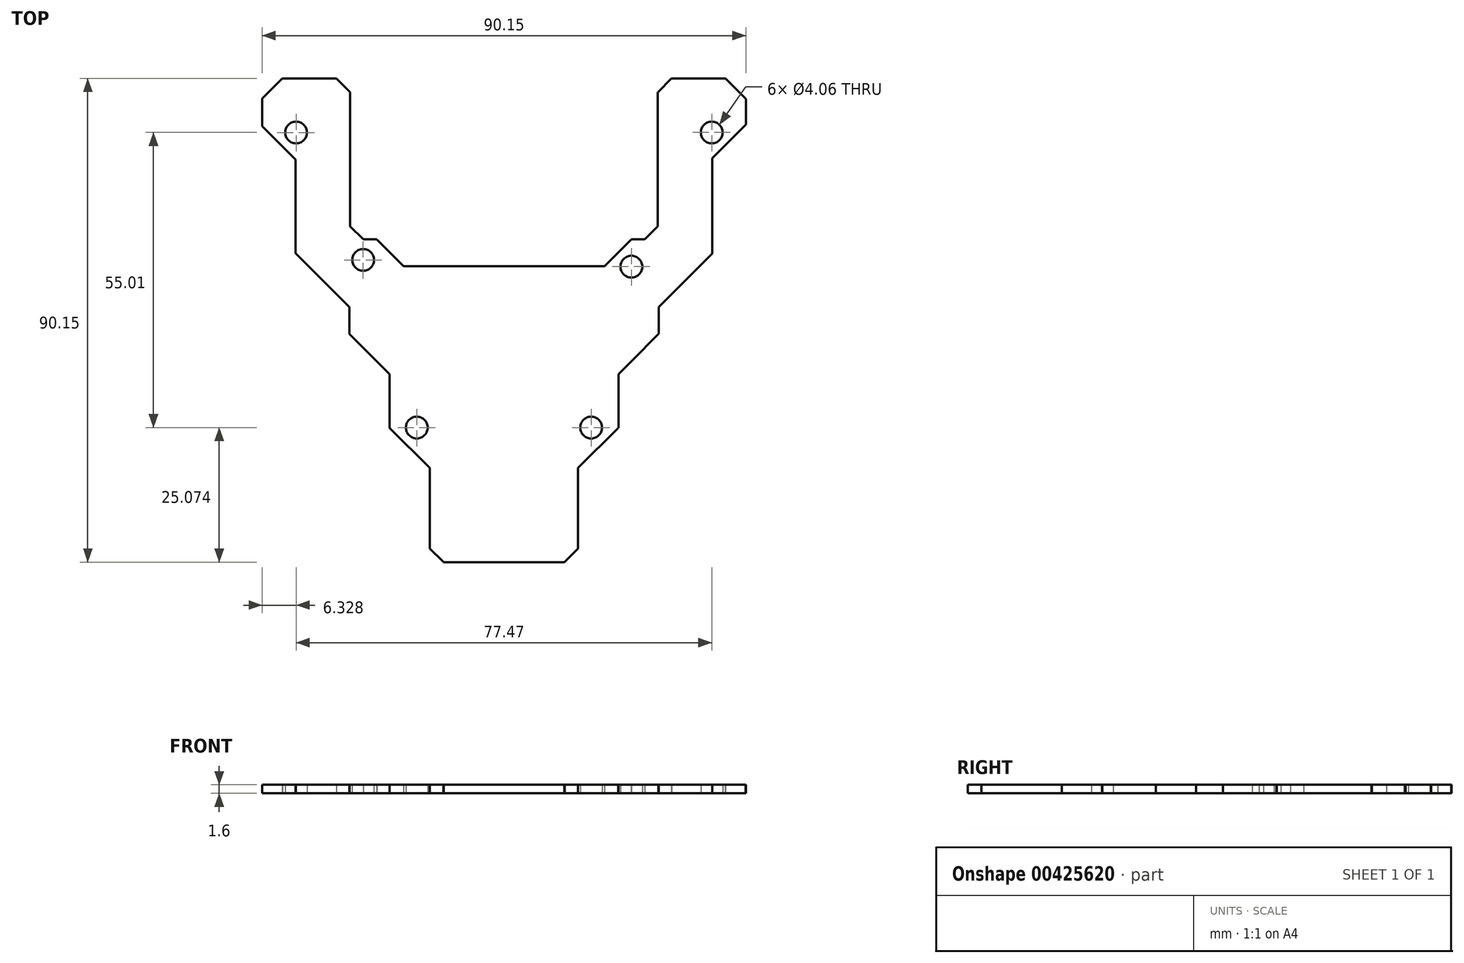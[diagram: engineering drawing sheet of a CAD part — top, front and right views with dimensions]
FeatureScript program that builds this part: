
annotation { "Feature Type Name" : "Feature", "Feature Type Description" : "" }
export const myFeature = defineFeature(function(context is Context, id is Id, definition is map)
    precondition{}
    {
        {
            var Q0;
            Q0=qCreatedBy(makeId("Top.planeOp"),FACE);
            var sketch = newSketch(context, id + "F0", { "sketchPlane" : qUnion([Q0])});
            skCircle(sketch, "E0", {"center": v(38.73, 22.84) * mm, "radius": 2.03 * mm});
            skCircle(sketch, "E1", {"center": v(23.76, -2.17) * mm, "radius": 2.03 * mm});
            skCircle(sketch, "E2", {"center": v(16.26, -32.17) * mm, "radius": 2.03 * mm});
            skCircle(sketch, "E3", {"center": v(-16.24, -32.17) * mm, "radius": 2.03 * mm});
            skCircle(sketch, "E4", {"center": v(-26.24, -0.92) * mm, "radius": 2.03 * mm});
            skCircle(sketch, "E5", {"center": v(-38.74, 22.83) * mm, "radius": 2.03 * mm});
            skLineSegment(sketch, "E6", {"start": v(-31.24, 32.9) * mm, "end": v(-31.24, 32.9) * mm});
            skLineSegment(sketch, "E7", {"start": v(-41.24, 32.9) * mm, "end": v(-31.24, 32.9) * mm});
            skLineSegment(sketch, "E8", {"start": v(-41.24, 32.9) * mm, "end": v(-41.24, 32.9) * mm});
            skLineSegment(sketch, "E9", {"start": v(-41.25, 32.9) * mm, "end": v(-41.24, 32.9) * mm});
            skLineSegment(sketch, "E10", {"start": v(-41.26, 32.9) * mm, "end": v(-41.25, 32.9) * mm});
            skLineSegment(sketch, "E11", {"start": v(-41.27, 32.9) * mm, "end": v(-41.26, 32.9) * mm});
            skLineSegment(sketch, "E12", {"start": v(-41.27, 32.9) * mm, "end": v(-41.27, 32.9) * mm});
            skLineSegment(sketch, "E13", {"start": v(-41.28, 32.9) * mm, "end": v(-41.27, 32.9) * mm});
            skLineSegment(sketch, "E14", {"start": v(-41.29, 32.9) * mm, "end": v(-41.28, 32.9) * mm});
            skLineSegment(sketch, "E15", {"start": v(-41.3, 32.89) * mm, "end": v(-41.29, 32.9) * mm});
            skLineSegment(sketch, "E16", {"start": v(-41.3, 32.89) * mm, "end": v(-41.3, 32.89) * mm});
            skLineSegment(sketch, "E17", {"start": v(-45.04, 29.14) * mm, "end": v(-41.3, 32.89) * mm});
            skLineSegment(sketch, "E18", {"start": v(-45.05, 29.13) * mm, "end": v(-45.04, 29.14) * mm});
            skLineSegment(sketch, "E19", {"start": v(-45.05, 29.13) * mm, "end": v(-45.05, 29.13) * mm});
            skLineSegment(sketch, "E20", {"start": v(-45.05, 29.12) * mm, "end": v(-45.05, 29.13) * mm});
            skLineSegment(sketch, "E21", {"start": v(-45.06, 29.12) * mm, "end": v(-45.05, 29.12) * mm});
            skLineSegment(sketch, "E22", {"start": v(-45.06, 29.11) * mm, "end": v(-45.06, 29.12) * mm});
            skLineSegment(sketch, "E23", {"start": v(-45.06, 29.11) * mm, "end": v(-45.06, 29.11) * mm});
            skLineSegment(sketch, "E24", {"start": v(-45.06, 29.1) * mm, "end": v(-45.06, 29.11) * mm});
            skLineSegment(sketch, "E25", {"start": v(-45.07, 29.1) * mm, "end": v(-45.06, 29.1) * mm});
            skLineSegment(sketch, "E26", {"start": v(-45.07, 29.09) * mm, "end": v(-45.07, 29.1) * mm});
            skLineSegment(sketch, "E27", {"start": v(-45.07, 29.08) * mm, "end": v(-45.07, 29.09) * mm});
            skLineSegment(sketch, "E28", {"start": v(-45.07, 24.08) * mm, "end": v(-45.07, 29.08) * mm});
            skLineSegment(sketch, "E29", {"start": v(-45.07, 24.08) * mm, "end": v(-45.07, 24.08) * mm});
            skLineSegment(sketch, "E30", {"start": v(-45.06, 24.07) * mm, "end": v(-45.07, 24.08) * mm});
            skLineSegment(sketch, "E31", {"start": v(-45.06, 24.06) * mm, "end": v(-45.06, 24.07) * mm});
            skLineSegment(sketch, "E32", {"start": v(-45.06, 24.06) * mm, "end": v(-45.06, 24.06) * mm});
            skLineSegment(sketch, "E33", {"start": v(-45.06, 24.05) * mm, "end": v(-45.06, 24.06) * mm});
            skLineSegment(sketch, "E34", {"start": v(-45.05, 24.04) * mm, "end": v(-45.06, 24.05) * mm});
            skLineSegment(sketch, "E35", {"start": v(-45.05, 24.04) * mm, "end": v(-45.05, 24.04) * mm});
            skLineSegment(sketch, "E36", {"start": v(-45.05, 24.03) * mm, "end": v(-45.05, 24.04) * mm});
            skLineSegment(sketch, "E37", {"start": v(-45.04, 24.03) * mm, "end": v(-45.05, 24.03) * mm});
            skLineSegment(sketch, "E38", {"start": v(-38.82, 17.8) * mm, "end": v(-45.04, 24.03) * mm});
            skLineSegment(sketch, "E39", {"start": v(-38.82, 0.33) * mm, "end": v(-38.82, 17.8) * mm});
            skLineSegment(sketch, "E40", {"start": v(-38.82, 0.33) * mm, "end": v(-38.82, 0.33) * mm});
            skLineSegment(sketch, "E41", {"start": v(-38.81, 0.32) * mm, "end": v(-38.82, 0.33) * mm});
            skLineSegment(sketch, "E42", {"start": v(-38.81, 0.3) * mm, "end": v(-38.81, 0.32) * mm});
            skLineSegment(sketch, "E43", {"start": v(-38.81, 0.3) * mm, "end": v(-38.81, 0.3) * mm});
            skLineSegment(sketch, "E44", {"start": v(-38.8, 0.3) * mm, "end": v(-38.81, 0.3) * mm});
            skLineSegment(sketch, "E45", {"start": v(-38.8, 0.3) * mm, "end": v(-38.8, 0.3) * mm});
            skLineSegment(sketch, "E46", {"start": v(-38.8, 0.29) * mm, "end": v(-38.8, 0.3) * mm});
            skLineSegment(sketch, "E47", {"start": v(-38.8, 0.28) * mm, "end": v(-38.8, 0.29) * mm});
            skLineSegment(sketch, "E48", {"start": v(-38.8, 0.28) * mm, "end": v(-38.8, 0.28) * mm});
            skLineSegment(sketch, "E49", {"start": v(-28.82, -9.7) * mm, "end": v(-38.8, 0.28) * mm});
            skLineSegment(sketch, "E50", {"start": v(-28.82, -14.67) * mm, "end": v(-28.82, -9.7) * mm});
            skLineSegment(sketch, "E51", {"start": v(-28.82, -14.67) * mm, "end": v(-28.82, -14.67) * mm});
            skLineSegment(sketch, "E52", {"start": v(-28.81, -14.68) * mm, "end": v(-28.82, -14.67) * mm});
            skLineSegment(sketch, "E53", {"start": v(-28.81, -14.7) * mm, "end": v(-28.81, -14.68) * mm});
            skLineSegment(sketch, "E54", {"start": v(-28.81, -14.7) * mm, "end": v(-28.81, -14.7) * mm});
            skLineSegment(sketch, "E55", {"start": v(-28.8, -14.7) * mm, "end": v(-28.81, -14.7) * mm});
            skLineSegment(sketch, "E56", {"start": v(-28.8, -14.7) * mm, "end": v(-28.8, -14.7) * mm});
            skLineSegment(sketch, "E57", {"start": v(-28.8, -14.71) * mm, "end": v(-28.8, -14.7) * mm});
            skLineSegment(sketch, "E58", {"start": v(-28.8, -14.72) * mm, "end": v(-28.8, -14.71) * mm});
            skLineSegment(sketch, "E59", {"start": v(-28.8, -14.72) * mm, "end": v(-28.8, -14.72) * mm});
            skLineSegment(sketch, "E60", {"start": v(-23.8, -19.72) * mm, "end": v(-28.8, -14.72) * mm});
            skLineSegment(sketch, "E61", {"start": v(-21.32, -22.2) * mm, "end": v(-23.8, -19.72) * mm});
            skLineSegment(sketch, "E62", {"start": v(-21.32, -32.17) * mm, "end": v(-21.32, -22.2) * mm});
            skLineSegment(sketch, "E63", {"start": v(-21.32, -32.17) * mm, "end": v(-21.32, -32.17) * mm});
            skLineSegment(sketch, "E64", {"start": v(-21.31, -32.18) * mm, "end": v(-21.32, -32.17) * mm});
            skLineSegment(sketch, "E65", {"start": v(-21.31, -32.2) * mm, "end": v(-21.31, -32.18) * mm});
            skLineSegment(sketch, "E66", {"start": v(-21.3, -32.2) * mm, "end": v(-21.31, -32.2) * mm});
            skLineSegment(sketch, "E67", {"start": v(-21.3, -32.2) * mm, "end": v(-21.3, -32.2) * mm});
            skLineSegment(sketch, "E68", {"start": v(-21.3, -32.21) * mm, "end": v(-21.3, -32.2) * mm});
            skLineSegment(sketch, "E69", {"start": v(-21.3, -32.22) * mm, "end": v(-21.3, -32.21) * mm});
            skLineSegment(sketch, "E70", {"start": v(-21.3, -32.22) * mm, "end": v(-21.3, -32.22) * mm});
            skLineSegment(sketch, "E71", {"start": v(-13.82, -39.7) * mm, "end": v(-21.3, -32.22) * mm});
            skLineSegment(sketch, "E72", {"start": v(-13.82, -54.67) * mm, "end": v(-13.82, -39.7) * mm});
            skLineSegment(sketch, "E73", {"start": v(-13.82, -54.67) * mm, "end": v(-13.82, -54.67) * mm});
            skLineSegment(sketch, "E74", {"start": v(-13.81, -54.68) * mm, "end": v(-13.82, -54.67) * mm});
            skLineSegment(sketch, "E75", {"start": v(-13.81, -54.7) * mm, "end": v(-13.81, -54.68) * mm});
            skLineSegment(sketch, "E76", {"start": v(-13.8, -54.7) * mm, "end": v(-13.81, -54.7) * mm});
            skLineSegment(sketch, "E77", {"start": v(-13.8, -54.7) * mm, "end": v(-13.8, -54.7) * mm});
            skLineSegment(sketch, "E78", {"start": v(-13.8, -54.71) * mm, "end": v(-13.8, -54.7) * mm});
            skLineSegment(sketch, "E79", {"start": v(-13.8, -54.72) * mm, "end": v(-13.8, -54.71) * mm});
            skLineSegment(sketch, "E80", {"start": v(-13.8, -54.72) * mm, "end": v(-13.8, -54.72) * mm});
            skLineSegment(sketch, "E81", {"start": v(-11.3, -57.22) * mm, "end": v(-13.8, -54.72) * mm});
            skLineSegment(sketch, "E82", {"start": v(-11.3, -57.22) * mm, "end": v(-11.3, -57.22) * mm});
            skLineSegment(sketch, "E83", {"start": v(-11.29, -57.22) * mm, "end": v(-11.3, -57.22) * mm});
            skLineSegment(sketch, "E84", {"start": v(-11.28, -57.23) * mm, "end": v(-11.29, -57.22) * mm});
            skLineSegment(sketch, "E85", {"start": v(-11.27, -57.23) * mm, "end": v(-11.28, -57.23) * mm});
            skLineSegment(sketch, "E86", {"start": v(-11.27, -57.24) * mm, "end": v(-11.27, -57.23) * mm});
            skLineSegment(sketch, "E87", {"start": v(-11.26, -57.24) * mm, "end": v(-11.27, -57.24) * mm});
            skLineSegment(sketch, "E88", {"start": v(-11.25, -57.24) * mm, "end": v(-11.26, -57.24) * mm});
            skLineSegment(sketch, "E89", {"start": v(-11.24, -57.24) * mm, "end": v(-11.25, -57.24) * mm});
            skLineSegment(sketch, "E90", {"start": v(-11.24, -57.24) * mm, "end": v(-11.24, -57.24) * mm});
            skLineSegment(sketch, "E91", {"start": v(11.26, -57.24) * mm, "end": v(-11.24, -57.24) * mm});
            skLineSegment(sketch, "E92", {"start": v(11.26, -57.24) * mm, "end": v(11.26, -57.24) * mm});
            skLineSegment(sketch, "E93", {"start": v(11.27, -57.24) * mm, "end": v(11.26, -57.24) * mm});
            skLineSegment(sketch, "E94", {"start": v(11.27, -57.24) * mm, "end": v(11.27, -57.24) * mm});
            skLineSegment(sketch, "E95", {"start": v(11.28, -57.24) * mm, "end": v(11.27, -57.24) * mm});
            skLineSegment(sketch, "E96", {"start": v(11.3, -57.23) * mm, "end": v(11.28, -57.24) * mm});
            skLineSegment(sketch, "E97", {"start": v(11.3, -57.23) * mm, "end": v(11.3, -57.23) * mm});
            skLineSegment(sketch, "E98", {"start": v(11.3, -57.22) * mm, "end": v(11.3, -57.23) * mm});
            skLineSegment(sketch, "E99", {"start": v(11.3, -57.22) * mm, "end": v(11.3, -57.22) * mm});
            skLineSegment(sketch, "E100", {"start": v(11.31, -57.22) * mm, "end": v(11.3, -57.22) * mm});
            skLineSegment(sketch, "E101", {"start": v(13.81, -54.72) * mm, "end": v(11.31, -57.22) * mm});
            skLineSegment(sketch, "E102", {"start": v(13.81, -54.72) * mm, "end": v(13.81, -54.72) * mm});
            skLineSegment(sketch, "E103", {"start": v(13.82, -54.71) * mm, "end": v(13.81, -54.72) * mm});
            skLineSegment(sketch, "E104", {"start": v(13.82, -54.7) * mm, "end": v(13.82, -54.71) * mm});
            skLineSegment(sketch, "E105", {"start": v(13.83, -54.7) * mm, "end": v(13.82, -54.7) * mm});
            skLineSegment(sketch, "E106", {"start": v(13.83, -54.7) * mm, "end": v(13.83, -54.7) * mm});
            skLineSegment(sketch, "E107", {"start": v(13.83, -54.68) * mm, "end": v(13.83, -54.7) * mm});
            skLineSegment(sketch, "E108", {"start": v(13.83, -54.67) * mm, "end": v(13.83, -54.68) * mm});
            skLineSegment(sketch, "E109", {"start": v(13.83, -54.67) * mm, "end": v(13.83, -54.67) * mm});
            skLineSegment(sketch, "E110", {"start": v(13.83, -39.7) * mm, "end": v(13.83, -54.67) * mm});
            skLineSegment(sketch, "E111", {"start": v(21.31, -32.22) * mm, "end": v(13.83, -39.7) * mm});
            skLineSegment(sketch, "E112", {"start": v(21.31, -32.22) * mm, "end": v(21.31, -32.22) * mm});
            skLineSegment(sketch, "E113", {"start": v(21.32, -32.21) * mm, "end": v(21.31, -32.22) * mm});
            skLineSegment(sketch, "E114", {"start": v(21.32, -32.2) * mm, "end": v(21.32, -32.21) * mm});
            skLineSegment(sketch, "E115", {"start": v(21.33, -32.2) * mm, "end": v(21.32, -32.2) * mm});
            skLineSegment(sketch, "E116", {"start": v(21.33, -32.2) * mm, "end": v(21.33, -32.2) * mm});
            skLineSegment(sketch, "E117", {"start": v(21.33, -32.18) * mm, "end": v(21.33, -32.2) * mm});
            skLineSegment(sketch, "E118", {"start": v(21.33, -32.17) * mm, "end": v(21.33, -32.18) * mm});
            skLineSegment(sketch, "E119", {"start": v(21.33, -32.17) * mm, "end": v(21.33, -32.17) * mm});
            skLineSegment(sketch, "E120", {"start": v(21.33, -22.2) * mm, "end": v(21.33, -32.17) * mm});
            skLineSegment(sketch, "E121", {"start": v(23.81, -19.72) * mm, "end": v(21.33, -22.2) * mm});
            skLineSegment(sketch, "E122", {"start": v(28.81, -14.72) * mm, "end": v(23.81, -19.72) * mm});
            skLineSegment(sketch, "E123", {"start": v(28.81, -14.72) * mm, "end": v(28.81, -14.72) * mm});
            skLineSegment(sketch, "E124", {"start": v(28.82, -14.71) * mm, "end": v(28.81, -14.72) * mm});
            skLineSegment(sketch, "E125", {"start": v(28.82, -14.7) * mm, "end": v(28.82, -14.71) * mm});
            skLineSegment(sketch, "E126", {"start": v(28.83, -14.7) * mm, "end": v(28.82, -14.7) * mm});
            skLineSegment(sketch, "E127", {"start": v(28.83, -14.7) * mm, "end": v(28.83, -14.7) * mm});
            skLineSegment(sketch, "E128", {"start": v(28.83, -14.68) * mm, "end": v(28.83, -14.7) * mm});
            skLineSegment(sketch, "E129", {"start": v(28.83, -14.67) * mm, "end": v(28.83, -14.68) * mm});
            skLineSegment(sketch, "E130", {"start": v(28.83, -14.67) * mm, "end": v(28.83, -14.67) * mm});
            skLineSegment(sketch, "E131", {"start": v(28.83, -9.7) * mm, "end": v(28.83, -14.67) * mm});
            skLineSegment(sketch, "E132", {"start": v(38.81, 0.28) * mm, "end": v(28.83, -9.7) * mm});
            skLineSegment(sketch, "E133", {"start": v(38.81, 0.28) * mm, "end": v(38.81, 0.28) * mm});
            skLineSegment(sketch, "E134", {"start": v(38.82, 0.29) * mm, "end": v(38.81, 0.28) * mm});
            skLineSegment(sketch, "E135", {"start": v(38.82, 0.3) * mm, "end": v(38.82, 0.29) * mm});
            skLineSegment(sketch, "E136", {"start": v(38.83, 0.3) * mm, "end": v(38.82, 0.3) * mm});
            skLineSegment(sketch, "E137", {"start": v(38.83, 0.3) * mm, "end": v(38.83, 0.3) * mm});
            skLineSegment(sketch, "E138", {"start": v(38.83, 0.32) * mm, "end": v(38.83, 0.3) * mm});
            skLineSegment(sketch, "E139", {"start": v(38.83, 0.33) * mm, "end": v(38.83, 0.32) * mm});
            skLineSegment(sketch, "E140", {"start": v(38.83, 0.33) * mm, "end": v(38.83, 0.33) * mm});
            skLineSegment(sketch, "E141", {"start": v(38.83, 18.05) * mm, "end": v(38.83, 0.33) * mm});
            skLineSegment(sketch, "E142", {"start": v(45.06, 24.28) * mm, "end": v(38.83, 18.05) * mm});
            skLineSegment(sketch, "E143", {"start": v(45.06, 24.28) * mm, "end": v(45.06, 24.28) * mm});
            skLineSegment(sketch, "E144", {"start": v(45.07, 24.29) * mm, "end": v(45.06, 24.28) * mm});
            skLineSegment(sketch, "E145", {"start": v(45.07, 24.3) * mm, "end": v(45.07, 24.29) * mm});
            skLineSegment(sketch, "E146", {"start": v(45.08, 24.3) * mm, "end": v(45.07, 24.3) * mm});
            skLineSegment(sketch, "E147", {"start": v(45.08, 24.3) * mm, "end": v(45.08, 24.3) * mm});
            skLineSegment(sketch, "E148", {"start": v(45.08, 24.32) * mm, "end": v(45.08, 24.3) * mm});
            skLineSegment(sketch, "E149", {"start": v(45.08, 24.33) * mm, "end": v(45.08, 24.32) * mm});
            skLineSegment(sketch, "E150", {"start": v(45.08, 24.33) * mm, "end": v(45.08, 24.33) * mm});
            skLineSegment(sketch, "E151", {"start": v(45.08, 29.08) * mm, "end": v(45.08, 24.33) * mm});
            skLineSegment(sketch, "E152", {"start": v(45.08, 29.09) * mm, "end": v(45.08, 29.08) * mm});
            skLineSegment(sketch, "E153", {"start": v(45.08, 29.1) * mm, "end": v(45.08, 29.09) * mm});
            skLineSegment(sketch, "E154", {"start": v(45.08, 29.1) * mm, "end": v(45.08, 29.1) * mm});
            skLineSegment(sketch, "E155", {"start": v(45.08, 29.11) * mm, "end": v(45.08, 29.1) * mm});
            skLineSegment(sketch, "E156", {"start": v(45.08, 29.11) * mm, "end": v(45.08, 29.11) * mm});
            skLineSegment(sketch, "E157", {"start": v(45.08, 29.12) * mm, "end": v(45.08, 29.11) * mm});
            skLineSegment(sketch, "E158", {"start": v(45.07, 29.12) * mm, "end": v(45.08, 29.12) * mm});
            skLineSegment(sketch, "E159", {"start": v(45.07, 29.13) * mm, "end": v(45.07, 29.12) * mm});
            skLineSegment(sketch, "E160", {"start": v(45.06, 29.13) * mm, "end": v(45.07, 29.13) * mm});
            skLineSegment(sketch, "E161", {"start": v(45.06, 29.14) * mm, "end": v(45.06, 29.13) * mm});
            skLineSegment(sketch, "E162", {"start": v(41.31, 32.89) * mm, "end": v(45.06, 29.14) * mm});
            skLineSegment(sketch, "E163", {"start": v(41.3, 32.89) * mm, "end": v(41.31, 32.89) * mm});
            skLineSegment(sketch, "E164", {"start": v(41.3, 32.9) * mm, "end": v(41.3, 32.89) * mm});
            skLineSegment(sketch, "E165", {"start": v(41.3, 32.9) * mm, "end": v(41.3, 32.9) * mm});
            skLineSegment(sketch, "E166", {"start": v(41.29, 32.9) * mm, "end": v(41.3, 32.9) * mm});
            skLineSegment(sketch, "E167", {"start": v(41.28, 32.9) * mm, "end": v(41.29, 32.9) * mm});
            skLineSegment(sketch, "E168", {"start": v(41.27, 32.9) * mm, "end": v(41.28, 32.9) * mm});
            skLineSegment(sketch, "E169", {"start": v(41.27, 32.9) * mm, "end": v(41.27, 32.9) * mm});
            skLineSegment(sketch, "E170", {"start": v(41.26, 32.9) * mm, "end": v(41.27, 32.9) * mm});
            skLineSegment(sketch, "E171", {"start": v(41.26, 32.9) * mm, "end": v(41.26, 32.9) * mm});
            skLineSegment(sketch, "E172", {"start": v(31.26, 32.9) * mm, "end": v(41.26, 32.9) * mm});
            skLineSegment(sketch, "E173", {"start": v(31.26, 32.9) * mm, "end": v(31.26, 32.9) * mm});
            skLineSegment(sketch, "E174", {"start": v(31.25, 32.9) * mm, "end": v(31.26, 32.9) * mm});
            skLineSegment(sketch, "E175", {"start": v(31.24, 32.9) * mm, "end": v(31.25, 32.9) * mm});
            skLineSegment(sketch, "E176", {"start": v(31.23, 32.9) * mm, "end": v(31.24, 32.9) * mm});
            skLineSegment(sketch, "E177", {"start": v(31.23, 32.9) * mm, "end": v(31.23, 32.9) * mm});
            skLineSegment(sketch, "E178", {"start": v(31.22, 32.9) * mm, "end": v(31.23, 32.9) * mm});
            skLineSegment(sketch, "E179", {"start": v(31.21, 32.9) * mm, "end": v(31.22, 32.9) * mm});
            skLineSegment(sketch, "E180", {"start": v(31.2, 32.89) * mm, "end": v(31.21, 32.9) * mm});
            skLineSegment(sketch, "E181", {"start": v(31.2, 32.89) * mm, "end": v(31.2, 32.89) * mm});
            skLineSegment(sketch, "E182", {"start": v(28.7, 30.39) * mm, "end": v(31.2, 32.89) * mm});
            skLineSegment(sketch, "E183", {"start": v(28.7, 30.38) * mm, "end": v(28.7, 30.39) * mm});
            skLineSegment(sketch, "E184", {"start": v(28.7, 30.38) * mm, "end": v(28.7, 30.38) * mm});
            skLineSegment(sketch, "E185", {"start": v(28.7, 30.37) * mm, "end": v(28.7, 30.38) * mm});
            skLineSegment(sketch, "E186", {"start": v(28.7, 30.37) * mm, "end": v(28.7, 30.37) * mm});
            skLineSegment(sketch, "E187", {"start": v(28.69, 30.36) * mm, "end": v(28.7, 30.37) * mm});
            skLineSegment(sketch, "E188", {"start": v(28.69, 30.36) * mm, "end": v(28.69, 30.36) * mm});
            skLineSegment(sketch, "E189", {"start": v(28.69, 30.35) * mm, "end": v(28.69, 30.36) * mm});
            skLineSegment(sketch, "E190", {"start": v(28.68, 30.34) * mm, "end": v(28.69, 30.35) * mm});
            skLineSegment(sketch, "E191", {"start": v(28.68, 30.34) * mm, "end": v(28.68, 30.34) * mm});
            skLineSegment(sketch, "E192", {"start": v(28.68, 30.33) * mm, "end": v(28.68, 30.34) * mm});
            skLineSegment(sketch, "E193", {"start": v(28.68, 5.37) * mm, "end": v(28.68, 30.33) * mm});
            skLineSegment(sketch, "E194", {"start": v(26.23, 2.9) * mm, "end": v(28.68, 5.37) * mm});
            skLineSegment(sketch, "E195", {"start": v(23.76, 2.9) * mm, "end": v(26.23, 2.9) * mm});
            skLineSegment(sketch, "E196", {"start": v(23.76, 2.9) * mm, "end": v(23.76, 2.9) * mm});
            skLineSegment(sketch, "E197", {"start": v(23.75, 2.9) * mm, "end": v(23.76, 2.9) * mm});
            skLineSegment(sketch, "E198", {"start": v(23.74, 2.9) * mm, "end": v(23.75, 2.9) * mm});
            skLineSegment(sketch, "E199", {"start": v(23.73, 2.9) * mm, "end": v(23.74, 2.9) * mm});
            skLineSegment(sketch, "E200", {"start": v(23.73, 2.9) * mm, "end": v(23.73, 2.9) * mm});
            skLineSegment(sketch, "E201", {"start": v(23.72, 2.9) * mm, "end": v(23.73, 2.9) * mm});
            skLineSegment(sketch, "E202", {"start": v(23.71, 2.9) * mm, "end": v(23.72, 2.9) * mm});
            skLineSegment(sketch, "E203", {"start": v(23.7, 2.89) * mm, "end": v(23.71, 2.9) * mm});
            skLineSegment(sketch, "E204", {"start": v(23.7, 2.89) * mm, "end": v(23.7, 2.89) * mm});
            skLineSegment(sketch, "E205", {"start": v(18.73, -2.1) * mm, "end": v(23.7, 2.89) * mm});
            skLineSegment(sketch, "E206", {"start": v(-18.71, -2.1) * mm, "end": v(18.73, -2.1) * mm});
            skLineSegment(sketch, "E207", {"start": v(-23.69, 2.89) * mm, "end": v(-18.71, -2.1) * mm});
            skLineSegment(sketch, "E208", {"start": v(-23.7, 2.89) * mm, "end": v(-23.69, 2.89) * mm});
            skLineSegment(sketch, "E209", {"start": v(-23.7, 2.9) * mm, "end": v(-23.7, 2.89) * mm});
            skLineSegment(sketch, "E210", {"start": v(-23.7, 2.9) * mm, "end": v(-23.7, 2.9) * mm});
            skLineSegment(sketch, "E211", {"start": v(-23.71, 2.9) * mm, "end": v(-23.7, 2.9) * mm});
            skLineSegment(sketch, "E212", {"start": v(-23.72, 2.9) * mm, "end": v(-23.71, 2.9) * mm});
            skLineSegment(sketch, "E213", {"start": v(-23.73, 2.9) * mm, "end": v(-23.72, 2.9) * mm});
            skLineSegment(sketch, "E214", {"start": v(-23.73, 2.9) * mm, "end": v(-23.73, 2.9) * mm});
            skLineSegment(sketch, "E215", {"start": v(-23.74, 2.9) * mm, "end": v(-23.73, 2.9) * mm});
            skLineSegment(sketch, "E216", {"start": v(-23.74, 2.9) * mm, "end": v(-23.74, 2.9) * mm});
            skLineSegment(sketch, "E217", {"start": v(-26.21, 2.9) * mm, "end": v(-23.74, 2.9) * mm});
            skLineSegment(sketch, "E218", {"start": v(-28.67, 5.37) * mm, "end": v(-26.21, 2.9) * mm});
            skLineSegment(sketch, "E219", {"start": v(-28.67, 30.33) * mm, "end": v(-28.67, 5.37) * mm});
            skLineSegment(sketch, "E220", {"start": v(-28.67, 30.34) * mm, "end": v(-28.67, 30.33) * mm});
            skLineSegment(sketch, "E221", {"start": v(-28.67, 30.34) * mm, "end": v(-28.67, 30.34) * mm});
            skLineSegment(sketch, "E222", {"start": v(-28.67, 30.35) * mm, "end": v(-28.67, 30.34) * mm});
            skLineSegment(sketch, "E223", {"start": v(-28.67, 30.36) * mm, "end": v(-28.67, 30.35) * mm});
            skLineSegment(sketch, "E224", {"start": v(-28.67, 30.36) * mm, "end": v(-28.67, 30.36) * mm});
            skLineSegment(sketch, "E225", {"start": v(-28.67, 30.37) * mm, "end": v(-28.67, 30.36) * mm});
            skLineSegment(sketch, "E226", {"start": v(-28.68, 30.37) * mm, "end": v(-28.67, 30.37) * mm});
            skLineSegment(sketch, "E227", {"start": v(-28.68, 30.38) * mm, "end": v(-28.68, 30.37) * mm});
            skLineSegment(sketch, "E228", {"start": v(-28.69, 30.38) * mm, "end": v(-28.68, 30.38) * mm});
            skLineSegment(sketch, "E229", {"start": v(-28.69, 30.39) * mm, "end": v(-28.69, 30.38) * mm});
            skLineSegment(sketch, "E230", {"start": v(-31.19, 32.89) * mm, "end": v(-28.69, 30.39) * mm});
            skLineSegment(sketch, "E231", {"start": v(-31.2, 32.89) * mm, "end": v(-31.19, 32.89) * mm});
            skLineSegment(sketch, "E232", {"start": v(-31.2, 32.9) * mm, "end": v(-31.2, 32.89) * mm});
            skLineSegment(sketch, "E233", {"start": v(-31.2, 32.9) * mm, "end": v(-31.2, 32.9) * mm});
            skLineSegment(sketch, "E234", {"start": v(-31.21, 32.9) * mm, "end": v(-31.2, 32.9) * mm});
            skLineSegment(sketch, "E235", {"start": v(-31.22, 32.9) * mm, "end": v(-31.21, 32.9) * mm});
            skLineSegment(sketch, "E236", {"start": v(-31.23, 32.9) * mm, "end": v(-31.22, 32.9) * mm});
            skLineSegment(sketch, "E237", {"start": v(-31.23, 32.9) * mm, "end": v(-31.23, 32.9) * mm});
            skLineSegment(sketch, "E238", {"start": v(-31.24, 32.9) * mm, "end": v(-31.23, 32.9) * mm});
            skLineSegment(sketch, "E239.0.1", {"start": v(-31.24, 32.9) * mm, "end": v(-41.24, 32.9) * mm});
            skLineSegment(sketch, "E239.0.3", {"start": v(-41.24, 32.9) * mm, "end": v(-41.25, 32.9) * mm});
            skLineSegment(sketch, "E239.0.4", {"start": v(-41.25, 32.9) * mm, "end": v(-41.26, 32.9) * mm});
            skLineSegment(sketch, "E239.0.5", {"start": v(-41.26, 32.9) * mm, "end": v(-41.27, 32.9) * mm});
            skLineSegment(sketch, "E239.0.8", {"start": v(-41.27, 32.9) * mm, "end": v(-41.28, 32.9) * mm});
            skLineSegment(sketch, "E239.0.9", {"start": v(-41.28, 32.9) * mm, "end": v(-41.29, 32.9) * mm});
            skLineSegment(sketch, "E239.0.10", {"start": v(-41.29, 32.9) * mm, "end": v(-41.3, 32.89) * mm});
            skLineSegment(sketch, "E239.0.12", {"start": v(-41.3, 32.89) * mm, "end": v(-45.04, 29.14) * mm});
            skLineSegment(sketch, "E239.0.13", {"start": v(-45.04, 29.14) * mm, "end": v(-45.05, 29.13) * mm});
            skLineSegment(sketch, "E239.0.15", {"start": v(-45.05, 29.13) * mm, "end": v(-45.05, 29.12) * mm});
            skLineSegment(sketch, "E239.0.16", {"start": v(-45.05, 29.12) * mm, "end": v(-45.06, 29.12) * mm});
            skLineSegment(sketch, "E239.0.17", {"start": v(-45.06, 29.12) * mm, "end": v(-45.06, 29.11) * mm});
            skLineSegment(sketch, "E239.0.19", {"start": v(-45.06, 29.11) * mm, "end": v(-45.06, 29.1) * mm});
            skLineSegment(sketch, "E239.0.20", {"start": v(-45.06, 29.1) * mm, "end": v(-45.07, 29.1) * mm});
            skLineSegment(sketch, "E239.0.21", {"start": v(-45.07, 29.1) * mm, "end": v(-45.07, 29.09) * mm});
            skLineSegment(sketch, "E239.0.22", {"start": v(-45.07, 29.09) * mm, "end": v(-45.07, 29.08) * mm});
            skLineSegment(sketch, "E239.0.23", {"start": v(-45.07, 29.08) * mm, "end": v(-45.07, 24.08) * mm});
            skLineSegment(sketch, "E239.0.26", {"start": v(-45.07, 24.08) * mm, "end": v(-45.06, 24.07) * mm});
            skLineSegment(sketch, "E239.0.27", {"start": v(-45.06, 24.07) * mm, "end": v(-45.06, 24.06) * mm});
            skLineSegment(sketch, "E239.0.29", {"start": v(-45.06, 24.06) * mm, "end": v(-45.06, 24.05) * mm});
            skLineSegment(sketch, "E239.0.30", {"start": v(-45.06, 24.05) * mm, "end": v(-45.05, 24.04) * mm});
            skLineSegment(sketch, "E239.0.32", {"start": v(-45.05, 24.04) * mm, "end": v(-45.05, 24.03) * mm});
            skLineSegment(sketch, "E239.0.33", {"start": v(-45.05, 24.03) * mm, "end": v(-45.04, 24.03) * mm});
            skLineSegment(sketch, "E239.0.34", {"start": v(-45.04, 24.03) * mm, "end": v(-38.82, 17.8) * mm});
            skLineSegment(sketch, "E239.0.35", {"start": v(-38.82, 17.8) * mm, "end": v(-38.82, 0.33) * mm});
            skLineSegment(sketch, "E239.0.38", {"start": v(-38.82, 0.33) * mm, "end": v(-38.81, 0.32) * mm});
            skLineSegment(sketch, "E239.0.39", {"start": v(-38.81, 0.32) * mm, "end": v(-38.81, 0.3) * mm});
            skLineSegment(sketch, "E239.0.41", {"start": v(-38.81, 0.3) * mm, "end": v(-38.8, 0.3) * mm});
            skLineSegment(sketch, "E239.0.43", {"start": v(-38.8, 0.3) * mm, "end": v(-38.8, 0.29) * mm});
            skLineSegment(sketch, "E239.0.44", {"start": v(-38.8, 0.29) * mm, "end": v(-38.8, 0.28) * mm});
            skLineSegment(sketch, "E239.0.46", {"start": v(-38.8, 0.28) * mm, "end": v(-28.82, -9.7) * mm});
            skLineSegment(sketch, "E239.0.47", {"start": v(-28.82, -9.7) * mm, "end": v(-28.82, -14.67) * mm});
            skLineSegment(sketch, "E239.0.50", {"start": v(-28.82, -14.67) * mm, "end": v(-28.81, -14.68) * mm});
            skLineSegment(sketch, "E239.0.51", {"start": v(-28.81, -14.68) * mm, "end": v(-28.81, -14.7) * mm});
            skLineSegment(sketch, "E239.0.53", {"start": v(-28.81, -14.7) * mm, "end": v(-28.8, -14.7) * mm});
            skLineSegment(sketch, "E239.0.55", {"start": v(-28.8, -14.7) * mm, "end": v(-28.8, -14.71) * mm});
            skLineSegment(sketch, "E239.0.56", {"start": v(-28.8, -14.71) * mm, "end": v(-28.8, -14.72) * mm});
            skLineSegment(sketch, "E239.0.58", {"start": v(-28.8, -14.72) * mm, "end": v(-23.8, -19.72) * mm});
            skLineSegment(sketch, "E239.0.59", {"start": v(-23.8, -19.72) * mm, "end": v(-21.32, -22.2) * mm});
            skLineSegment(sketch, "E239.0.60", {"start": v(-21.32, -22.2) * mm, "end": v(-21.32, -32.17) * mm});
            skLineSegment(sketch, "E239.0.63", {"start": v(-21.32, -32.17) * mm, "end": v(-21.31, -32.18) * mm});
            skLineSegment(sketch, "E239.0.64", {"start": v(-21.31, -32.18) * mm, "end": v(-21.31, -32.2) * mm});
            skLineSegment(sketch, "E239.0.65", {"start": v(-21.31, -32.2) * mm, "end": v(-21.3, -32.2) * mm});
            skLineSegment(sketch, "E239.0.67", {"start": v(-21.3, -32.2) * mm, "end": v(-21.3, -32.21) * mm});
            skLineSegment(sketch, "E239.0.68", {"start": v(-21.3, -32.21) * mm, "end": v(-21.3, -32.22) * mm});
            skLineSegment(sketch, "E239.0.70", {"start": v(-21.3, -32.22) * mm, "end": v(-13.82, -39.7) * mm});
            skLineSegment(sketch, "E239.0.71", {"start": v(-13.82, -39.7) * mm, "end": v(-13.82, -54.67) * mm});
            skLineSegment(sketch, "E239.0.74", {"start": v(-13.82, -54.67) * mm, "end": v(-13.81, -54.68) * mm});
            skLineSegment(sketch, "E239.0.75", {"start": v(-13.81, -54.68) * mm, "end": v(-13.81, -54.7) * mm});
            skLineSegment(sketch, "E239.0.76", {"start": v(-13.81, -54.7) * mm, "end": v(-13.8, -54.7) * mm});
            skLineSegment(sketch, "E239.0.78", {"start": v(-13.8, -54.7) * mm, "end": v(-13.8, -54.71) * mm});
            skLineSegment(sketch, "E239.0.79", {"start": v(-13.8, -54.71) * mm, "end": v(-13.8, -54.72) * mm});
            skLineSegment(sketch, "E239.0.81", {"start": v(-13.8, -54.72) * mm, "end": v(-11.3, -57.22) * mm});
            skLineSegment(sketch, "E239.0.83", {"start": v(-11.3, -57.22) * mm, "end": v(-11.29, -57.22) * mm});
            skLineSegment(sketch, "E239.0.84", {"start": v(-11.29, -57.22) * mm, "end": v(-11.28, -57.23) * mm});
            skLineSegment(sketch, "E239.0.85", {"start": v(-11.28, -57.23) * mm, "end": v(-11.27, -57.23) * mm});
            skLineSegment(sketch, "E239.0.86", {"start": v(-11.27, -57.23) * mm, "end": v(-11.27, -57.24) * mm});
            skLineSegment(sketch, "E239.0.87", {"start": v(-11.27, -57.24) * mm, "end": v(-11.26, -57.24) * mm});
            skLineSegment(sketch, "E239.0.88", {"start": v(-11.26, -57.24) * mm, "end": v(-11.25, -57.24) * mm});
            skLineSegment(sketch, "E239.0.89", {"start": v(-11.25, -57.24) * mm, "end": v(-11.24, -57.24) * mm});
            skLineSegment(sketch, "E239.0.91", {"start": v(-11.24, -57.24) * mm, "end": v(11.26, -57.24) * mm});
            skLineSegment(sketch, "E239.0.93", {"start": v(11.26, -57.24) * mm, "end": v(11.27, -57.24) * mm});
            skLineSegment(sketch, "E239.0.95", {"start": v(11.27, -57.24) * mm, "end": v(11.28, -57.24) * mm});
            skLineSegment(sketch, "E239.0.96", {"start": v(11.28, -57.24) * mm, "end": v(11.3, -57.23) * mm});
            skLineSegment(sketch, "E239.0.98", {"start": v(11.3, -57.23) * mm, "end": v(11.3, -57.22) * mm});
            skLineSegment(sketch, "E239.0.100", {"start": v(11.3, -57.22) * mm, "end": v(11.31, -57.22) * mm});
            skLineSegment(sketch, "E239.0.101", {"start": v(11.31, -57.22) * mm, "end": v(13.81, -54.72) * mm});
            skLineSegment(sketch, "E239.0.103", {"start": v(13.81, -54.72) * mm, "end": v(13.82, -54.71) * mm});
            skLineSegment(sketch, "E239.0.104", {"start": v(13.82, -54.71) * mm, "end": v(13.82, -54.7) * mm});
            skLineSegment(sketch, "E239.0.105", {"start": v(13.82, -54.7) * mm, "end": v(13.83, -54.7) * mm});
            skLineSegment(sketch, "E239.0.107", {"start": v(13.83, -54.7) * mm, "end": v(13.83, -54.68) * mm});
            skLineSegment(sketch, "E239.0.108", {"start": v(13.83, -54.68) * mm, "end": v(13.83, -54.67) * mm});
            skLineSegment(sketch, "E239.0.111", {"start": v(13.83, -54.67) * mm, "end": v(13.83, -39.7) * mm});
            skLineSegment(sketch, "E239.0.112", {"start": v(13.83, -39.7) * mm, "end": v(21.31, -32.22) * mm});
            skLineSegment(sketch, "E239.0.114", {"start": v(21.31, -32.22) * mm, "end": v(21.32, -32.21) * mm});
            skLineSegment(sketch, "E239.0.115", {"start": v(21.32, -32.21) * mm, "end": v(21.32, -32.2) * mm});
            skLineSegment(sketch, "E239.0.116", {"start": v(21.32, -32.2) * mm, "end": v(21.33, -32.2) * mm});
            skLineSegment(sketch, "E239.0.118", {"start": v(21.33, -32.2) * mm, "end": v(21.33, -32.18) * mm});
            skLineSegment(sketch, "E239.0.119", {"start": v(21.33, -32.18) * mm, "end": v(21.33, -32.17) * mm});
            skLineSegment(sketch, "E239.0.122", {"start": v(21.33, -32.17) * mm, "end": v(21.33, -22.2) * mm});
            skLineSegment(sketch, "E239.0.123", {"start": v(21.33, -22.2) * mm, "end": v(23.81, -19.72) * mm});
            skLineSegment(sketch, "E239.0.124", {"start": v(23.81, -19.72) * mm, "end": v(28.81, -14.72) * mm});
            skLineSegment(sketch, "E239.0.126", {"start": v(28.81, -14.72) * mm, "end": v(28.82, -14.71) * mm});
            skLineSegment(sketch, "E239.0.127", {"start": v(28.82, -14.71) * mm, "end": v(28.82, -14.7) * mm});
            skLineSegment(sketch, "E239.0.128", {"start": v(28.82, -14.7) * mm, "end": v(28.83, -14.7) * mm});
            skLineSegment(sketch, "E239.0.131", {"start": v(28.83, -14.7) * mm, "end": v(28.83, -14.68) * mm});
            skLineSegment(sketch, "E239.0.132", {"start": v(28.83, -14.68) * mm, "end": v(28.83, -14.67) * mm});
            skLineSegment(sketch, "E239.0.135", {"start": v(28.83, -14.67) * mm, "end": v(28.83, -9.7) * mm});
            skLineSegment(sketch, "E239.0.136", {"start": v(28.83, -9.7) * mm, "end": v(38.81, 0.28) * mm});
            skLineSegment(sketch, "E239.0.138", {"start": v(38.81, 0.28) * mm, "end": v(38.82, 0.29) * mm});
            skLineSegment(sketch, "E239.0.139", {"start": v(38.82, 0.29) * mm, "end": v(38.82, 0.3) * mm});
            skLineSegment(sketch, "E239.0.140", {"start": v(38.82, 0.3) * mm, "end": v(38.83, 0.3) * mm});
            skLineSegment(sketch, "E239.0.143", {"start": v(38.83, 0.3) * mm, "end": v(38.83, 0.32) * mm});
            skLineSegment(sketch, "E239.0.144", {"start": v(38.83, 0.32) * mm, "end": v(38.83, 0.33) * mm});
            skLineSegment(sketch, "E239.0.147", {"start": v(38.83, 0.33) * mm, "end": v(38.83, 18.05) * mm});
            skLineSegment(sketch, "E239.0.148", {"start": v(38.83, 18.05) * mm, "end": v(45.06, 24.28) * mm});
            skLineSegment(sketch, "E239.0.150", {"start": v(45.06, 24.28) * mm, "end": v(45.07, 24.29) * mm});
            skLineSegment(sketch, "E239.0.151", {"start": v(45.07, 24.29) * mm, "end": v(45.07, 24.3) * mm});
            skLineSegment(sketch, "E239.0.152", {"start": v(45.07, 24.3) * mm, "end": v(45.08, 24.3) * mm});
            skLineSegment(sketch, "E239.0.155", {"start": v(45.08, 24.3) * mm, "end": v(45.08, 24.32) * mm});
            skLineSegment(sketch, "E239.0.156", {"start": v(45.08, 24.32) * mm, "end": v(45.08, 24.33) * mm});
            skLineSegment(sketch, "E239.0.159", {"start": v(45.08, 24.33) * mm, "end": v(45.08, 29.08) * mm});
            skLineSegment(sketch, "E239.0.160", {"start": v(45.08, 29.08) * mm, "end": v(45.08, 29.09) * mm});
            skLineSegment(sketch, "E239.0.161", {"start": v(45.08, 29.09) * mm, "end": v(45.08, 29.1) * mm});
            skLineSegment(sketch, "E239.0.163", {"start": v(45.08, 29.1) * mm, "end": v(45.08, 29.11) * mm});
            skLineSegment(sketch, "E239.0.165", {"start": v(45.08, 29.11) * mm, "end": v(45.08, 29.12) * mm});
            skLineSegment(sketch, "E239.0.166", {"start": v(45.08, 29.12) * mm, "end": v(45.07, 29.12) * mm});
            skLineSegment(sketch, "E239.0.167", {"start": v(45.07, 29.12) * mm, "end": v(45.07, 29.13) * mm});
            skLineSegment(sketch, "E239.0.168", {"start": v(45.07, 29.13) * mm, "end": v(45.06, 29.13) * mm});
            skLineSegment(sketch, "E239.0.169", {"start": v(45.06, 29.13) * mm, "end": v(45.06, 29.14) * mm});
            skLineSegment(sketch, "E239.0.170", {"start": v(45.06, 29.14) * mm, "end": v(41.31, 32.89) * mm});
            skLineSegment(sketch, "E239.0.171", {"start": v(41.31, 32.89) * mm, "end": v(41.3, 32.89) * mm});
            skLineSegment(sketch, "E239.0.172", {"start": v(41.3, 32.89) * mm, "end": v(41.3, 32.9) * mm});
            skLineSegment(sketch, "E239.0.175", {"start": v(41.3, 32.9) * mm, "end": v(41.29, 32.9) * mm});
            skLineSegment(sketch, "E239.0.176", {"start": v(41.29, 32.9) * mm, "end": v(41.28, 32.9) * mm});
            skLineSegment(sketch, "E239.0.177", {"start": v(41.28, 32.9) * mm, "end": v(41.27, 32.9) * mm});
            skLineSegment(sketch, "E239.0.179", {"start": v(41.27, 32.9) * mm, "end": v(41.26, 32.9) * mm});
            skLineSegment(sketch, "E239.0.181", {"start": v(41.26, 32.9) * mm, "end": v(31.26, 32.9) * mm});
            skLineSegment(sketch, "E239.0.183", {"start": v(31.26, 32.9) * mm, "end": v(31.25, 32.9) * mm});
            skLineSegment(sketch, "E239.0.184", {"start": v(31.25, 32.9) * mm, "end": v(31.24, 32.9) * mm});
            skLineSegment(sketch, "E239.0.185", {"start": v(31.24, 32.9) * mm, "end": v(31.23, 32.9) * mm});
            skLineSegment(sketch, "E239.0.188", {"start": v(31.23, 32.9) * mm, "end": v(31.22, 32.9) * mm});
            skLineSegment(sketch, "E239.0.189", {"start": v(31.22, 32.9) * mm, "end": v(31.21, 32.9) * mm});
            skLineSegment(sketch, "E239.0.190", {"start": v(31.21, 32.9) * mm, "end": v(31.2, 32.89) * mm});
            skLineSegment(sketch, "E239.0.192", {"start": v(31.2, 32.89) * mm, "end": v(28.7, 30.39) * mm});
            skLineSegment(sketch, "E239.0.193", {"start": v(28.7, 30.39) * mm, "end": v(28.7, 30.38) * mm});
            skLineSegment(sketch, "E239.0.195", {"start": v(28.7, 30.38) * mm, "end": v(28.7, 30.37) * mm});
            skLineSegment(sketch, "E239.0.197", {"start": v(28.7, 30.37) * mm, "end": v(28.69, 30.36) * mm});
            skLineSegment(sketch, "E239.0.199", {"start": v(28.69, 30.36) * mm, "end": v(28.69, 30.35) * mm});
            skLineSegment(sketch, "E239.0.200", {"start": v(28.69, 30.35) * mm, "end": v(28.68, 30.34) * mm});
            skLineSegment(sketch, "E239.0.202", {"start": v(28.68, 30.34) * mm, "end": v(28.68, 30.33) * mm});
            skLineSegment(sketch, "E239.0.203", {"start": v(28.68, 30.33) * mm, "end": v(28.68, 5.37) * mm});
            skLineSegment(sketch, "E239.0.204", {"start": v(28.68, 5.37) * mm, "end": v(26.23, 2.9) * mm});
            skLineSegment(sketch, "E239.0.205", {"start": v(26.23, 2.9) * mm, "end": v(23.76, 2.9) * mm});
            skLineSegment(sketch, "E239.0.207", {"start": v(23.76, 2.9) * mm, "end": v(23.75, 2.9) * mm});
            skLineSegment(sketch, "E239.0.208", {"start": v(23.75, 2.9) * mm, "end": v(23.74, 2.9) * mm});
            skLineSegment(sketch, "E239.0.209", {"start": v(23.74, 2.9) * mm, "end": v(23.73, 2.9) * mm});
            skLineSegment(sketch, "E239.0.212", {"start": v(23.73, 2.9) * mm, "end": v(23.72, 2.9) * mm});
            skLineSegment(sketch, "E239.0.213", {"start": v(23.72, 2.9) * mm, "end": v(23.71, 2.9) * mm});
            skLineSegment(sketch, "E239.0.214", {"start": v(23.71, 2.9) * mm, "end": v(23.7, 2.89) * mm});
            skLineSegment(sketch, "E239.0.216", {"start": v(23.7, 2.89) * mm, "end": v(18.73, -2.1) * mm});
            skLineSegment(sketch, "E239.0.217", {"start": v(18.73, -2.1) * mm, "end": v(-18.71, -2.1) * mm});
            skLineSegment(sketch, "E239.0.218", {"start": v(-18.71, -2.1) * mm, "end": v(-23.69, 2.89) * mm});
            skLineSegment(sketch, "E239.0.219", {"start": v(-23.69, 2.89) * mm, "end": v(-23.7, 2.89) * mm});
            skLineSegment(sketch, "E239.0.220", {"start": v(-23.7, 2.89) * mm, "end": v(-23.7, 2.9) * mm});
            skLineSegment(sketch, "E239.0.223", {"start": v(-23.7, 2.9) * mm, "end": v(-23.71, 2.9) * mm});
            skLineSegment(sketch, "E239.0.224", {"start": v(-23.71, 2.9) * mm, "end": v(-23.72, 2.9) * mm});
            skLineSegment(sketch, "E239.0.225", {"start": v(-23.72, 2.9) * mm, "end": v(-23.73, 2.9) * mm});
            skLineSegment(sketch, "E239.0.227", {"start": v(-23.73, 2.9) * mm, "end": v(-23.74, 2.9) * mm});
            skLineSegment(sketch, "E239.0.229", {"start": v(-23.74, 2.9) * mm, "end": v(-26.21, 2.9) * mm});
            skLineSegment(sketch, "E239.0.230", {"start": v(-26.21, 2.9) * mm, "end": v(-28.67, 5.37) * mm});
            skLineSegment(sketch, "E239.0.231", {"start": v(-28.67, 5.37) * mm, "end": v(-28.67, 30.33) * mm});
            skLineSegment(sketch, "E239.0.232", {"start": v(-28.67, 30.33) * mm, "end": v(-28.67, 30.34) * mm});
            skLineSegment(sketch, "E239.0.234", {"start": v(-28.67, 30.34) * mm, "end": v(-28.67, 30.35) * mm});
            skLineSegment(sketch, "E239.0.235", {"start": v(-28.67, 30.35) * mm, "end": v(-28.67, 30.36) * mm});
            skLineSegment(sketch, "E239.0.237", {"start": v(-28.67, 30.36) * mm, "end": v(-28.67, 30.37) * mm});
            skLineSegment(sketch, "E239.0.238", {"start": v(-28.67, 30.37) * mm, "end": v(-28.68, 30.37) * mm});
            skLineSegment(sketch, "E239.0.239", {"start": v(-28.68, 30.37) * mm, "end": v(-28.68, 30.38) * mm});
            skLineSegment(sketch, "E239.0.240", {"start": v(-28.68, 30.38) * mm, "end": v(-28.69, 30.38) * mm});
            skLineSegment(sketch, "E239.0.241", {"start": v(-28.69, 30.38) * mm, "end": v(-28.69, 30.39) * mm});
            skLineSegment(sketch, "E239.0.242", {"start": v(-28.69, 30.39) * mm, "end": v(-31.19, 32.89) * mm});
            skLineSegment(sketch, "E239.0.243", {"start": v(-31.19, 32.89) * mm, "end": v(-31.2, 32.89) * mm});
            skLineSegment(sketch, "E239.0.244", {"start": v(-31.2, 32.89) * mm, "end": v(-31.2, 32.9) * mm});
            skLineSegment(sketch, "E239.0.247", {"start": v(-31.2, 32.9) * mm, "end": v(-31.21, 32.9) * mm});
            skLineSegment(sketch, "E239.0.248", {"start": v(-31.21, 32.9) * mm, "end": v(-31.22, 32.9) * mm});
            skLineSegment(sketch, "E239.0.249", {"start": v(-31.22, 32.9) * mm, "end": v(-31.23, 32.9) * mm});
            skLineSegment(sketch, "E239.0.251", {"start": v(-31.23, 32.9) * mm, "end": v(-31.24, 32.9) * mm});
            skSolve(sketch);
        }
        {
            var Q0;
            Q0=makeQuery(id+"F0.imprint","IMPRINT",FACE,{"disambiguationData":[TD([[makeQuery(id+"F0.imprint","IMPRINT",EDGE,{"derivedFrom":sQuery(id+"F0.wireOp",EDGE,"E0")}),-1.0]])]});
            extrude(context, id + "F1", {"entities" : qUnion([Q0]), "depth" : 1.6 * mm, "offsetDistance" : 25 * mm});
        }
    });
